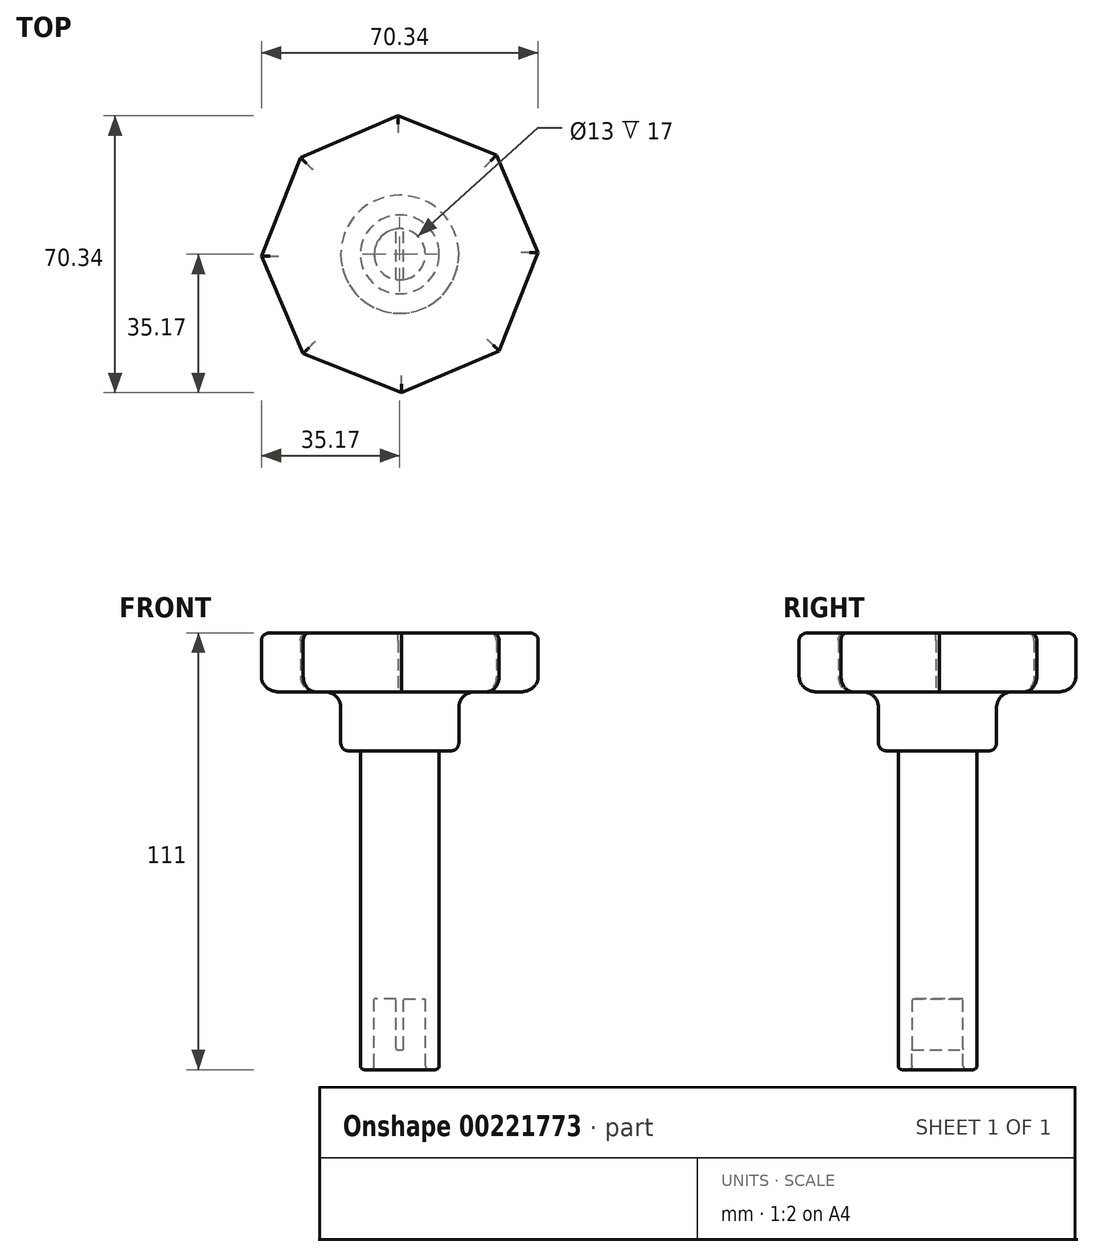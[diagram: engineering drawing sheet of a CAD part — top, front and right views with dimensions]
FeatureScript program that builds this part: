
annotation { "Feature Type Name" : "Feature", "Feature Type Description" : "" }
export const myFeature = defineFeature(function(context is Context, id is Id, definition is map)
    precondition{}
    {
        {
            var Q0;
            Q0=qCreatedBy(makeId("Top.planeOp"),FACE);
            var sketch = newSketch(context, id + "F0", { "sketchPlane" : qUnion([Q0])});
            skCircle(sketch, "E0.cCircle", {"center": v(0, 0) * mm, "radius": 32.5 * mm, "construction": true});
            skLineSegment(sketch, "E0.0", {"start": v(-25.21, 24.53) * mm, "end": v(-0.48, 35.17) * mm});
            skLineSegment(sketch, "E0.1", {"start": v(-0.48, 35.17) * mm, "end": v(24.53, 25.21) * mm});
            skLineSegment(sketch, "E0.2", {"start": v(24.53, 25.21) * mm, "end": v(35.17, 0.48) * mm});
            skLineSegment(sketch, "E0.3", {"start": v(35.17, 0.48) * mm, "end": v(25.21, -24.53) * mm});
            skLineSegment(sketch, "E0.4", {"start": v(25.21, -24.53) * mm, "end": v(0.48, -35.17) * mm});
            skLineSegment(sketch, "E0.5", {"start": v(0.48, -35.17) * mm, "end": v(-24.53, -25.21) * mm});
            skLineSegment(sketch, "E0.6", {"start": v(-24.53, -25.21) * mm, "end": v(-35.17, -0.48) * mm});
            skLineSegment(sketch, "E0.7", {"start": v(-35.17, -0.48) * mm, "end": v(-25.21, 24.53) * mm});
            skPoint(sketch, "E0.0.midPoint", {"position": v(-12.85, 29.85) * mm});
            skSolve(sketch);
        }
        {
            var Q0;
            Q0 = qSketchRegion(id + "F0", true);
            extrude(context, id + "F1", {"entities" : qUnion([Q0]), "depth" : 15 * mm});
        }
        {
            var Q0;
            Q0=makeQuery(id+"F1.opExtrude","CAP_FACE",FACE,{"disambiguationData":[OSD([sQuery(id+"F0.wireOp",EDGE,"E0.0"),sQuery(id+"F0.wireOp",EDGE,"E0.1"),sQuery(id+"F0.wireOp",EDGE,"E0.2"),sQuery(id+"F0.wireOp",EDGE,"E0.3"),sQuery(id+"F0.wireOp",EDGE,"E0.4"),sQuery(id+"F0.wireOp",EDGE,"E0.5"),sQuery(id+"F0.wireOp",EDGE,"E0.6"),sQuery(id+"F0.wireOp",EDGE,"E0.7")])],"isStart":true});
            var sketch = newSketch(context, id + "F2", { "sketchPlane" : qUnion([Q0])});
            skCircle(sketch, "E1", {"center": v(0, 0) * mm, "radius": 15 * mm});
            skSolve(sketch);
        }
        {
            var Q0;
            Q0 = qSketchRegion(id + "F2", true);
            extrude(context, id + "F3", {"entities" : qUnion([Q0]), "operationType" : NewBodyOperationType.ADD, "depth" : 15 * mm});
        }
        {
            var Q0;
            Q0=makeQuery(id+"F3.opExtrude","CAP_FACE",FACE,{"disambiguationData":[OSD([sQuery(id+"F2.wireOp",EDGE,"E1")])],"isStart":false});
            var sketch = newSketch(context, id + "F4", { "sketchPlane" : qUnion([Q0])});
            skCircle(sketch, "E2", {"center": v(0, 0) * mm, "radius": 10 * mm});
            skSolve(sketch);
        }
        {
            var Q0;
            Q0 = qSketchRegion(id + "F4", true);
            extrude(context, id + "F5", {"entities" : qUnion([Q0]), "operationType" : NewBodyOperationType.ADD, "depth" : 63 * mm});
        }
        {
            var Q0;
            Q0=makeQuery(id+"F5.opExtrude","CAP_EDGE",EDGE,{"disambiguationData":[OSD([sQuery(id+"F4.wireOp",EDGE,"E2")])],"isStart":true});
            var Q1;
            Q1=makeQuery(id+"F3.opExtrude","CAP_EDGE",EDGE,{"disambiguationData":[OSD([sQuery(id+"F2.wireOp",EDGE,"E1")])],"isStart":true});
            var Q2;
            Q2=makeQuery(id+"F1.opExtrude","CAP_FACE",FACE,{"disambiguationData":[OSD([sQuery(id+"F0.wireOp",EDGE,"E0.0"),sQuery(id+"F0.wireOp",EDGE,"E0.1"),sQuery(id+"F0.wireOp",EDGE,"E0.2"),sQuery(id+"F0.wireOp",EDGE,"E0.3"),sQuery(id+"F0.wireOp",EDGE,"E0.4"),sQuery(id+"F0.wireOp",EDGE,"E0.5"),sQuery(id+"F0.wireOp",EDGE,"E0.6"),sQuery(id+"F0.wireOp",EDGE,"E0.7")])],"isStart":true});
            fillet(context, id + "F6", {"entities" : qUnion([Q0, Q1, Q2]), "radius" : 4 * mm, "tangentPropagation" : true, "allowEdgeOverflow" : false});
        }
        {
            var Q0;
            Q0=makeQuery(id+"F1.opExtrude","CAP_FACE",FACE,{"disambiguationData":[OSD([sQuery(id+"F0.wireOp",EDGE,"E0.0"),sQuery(id+"F0.wireOp",EDGE,"E0.1"),sQuery(id+"F0.wireOp",EDGE,"E0.2"),sQuery(id+"F0.wireOp",EDGE,"E0.3"),sQuery(id+"F0.wireOp",EDGE,"E0.4"),sQuery(id+"F0.wireOp",EDGE,"E0.5"),sQuery(id+"F0.wireOp",EDGE,"E0.6"),sQuery(id+"F0.wireOp",EDGE,"E0.7")])],"isStart":false});
            var Q1;
            Q1=makeQuery(id+"F3.opExtrude","CAP_EDGE",EDGE,{"disambiguationData":[OSD([sQuery(id+"F2.wireOp",EDGE,"E1")])],"isStart":false});
            var Q2;
            Q2=makeQuery(id+"F3EO1j2PEONOvXl_1.opExtrude","CAP_EDGE",EDGE,{"disambiguationData":[OSD([sQuery(id+"FHGhLy2Cv9YmLs6_1.wireOp",EDGE,"M5NOvIKt-BTWJ-fP4f-TuiR-eHwRUutZLKey")])],"isStart":false});
            fillet(context, id + "F7", {"entities" : qUnion([Q0, Q1, Q2]), "radius" : 2 * mm, "tangentPropagation" : true, "allowEdgeOverflow" : false});
        }
        {
            var Q0;
            Q0=makeQuery(id+"F5.opExtrude","CAP_FACE",FACE,{"disambiguationData":[OSD([sQuery(id+"F4.wireOp",EDGE,"E2")])],"isStart":false});
            var sketch = newSketch(context, id + "F8", { "sketchPlane" : qUnion([Q0])});
            skCircle(sketch, "E3", {"center": v(0, 0) * mm, "radius": 10 * mm});
            skArc(sketch, "E4", {"start": v(-1, 6.42) * mm, "mid": v(-6.5, 0) * mm, "end": v(-1, -6.42) * mm});
            skLineSegment(sketch, "E5", {"start": v(-1, 6.42) * mm, "end": v(-1, -6.42) * mm});
            skLineSegment(sketch, "E6", {"start": v(1, 6.42) * mm, "end": v(1, -6.42) * mm});
            skArc(sketch, "E7.trimOffspring", {"start": v(1, -6.42) * mm, "mid": v(6.5, 0) * mm, "end": v(1, 6.42) * mm});
            skSolve(sketch);
        }
        {
            var Q0;
            Q0 = qSketchRegion(id + "F8", true);
            extrude(context, id + "F9", {"entities" : qUnion([Q0]), "operationType" : NewBodyOperationType.ADD, "depth" : 13 * mm});
        }
        {
            var Q0;
            Q0=makeQuery(id+"F9.opExtrude","CAP_EDGE",EDGE,{"disambiguationData":[OSD([sQuery(id+"F8.wireOp",EDGE,"E6")])],"isStart":false});
            var Q1;
            Q1=makeQuery(id+"F9.opExtrude","CAP_EDGE",EDGE,{"disambiguationData":[OSD([sQuery(id+"F8.wireOp",EDGE,"E5")])],"isStart":false});
            fillet(context, id + "F10", {"entities" : qUnion([Q0, Q1]), "radius" : .5 * mm, "tangentPropagation" : true, "allowEdgeOverflow" : false});
        }
        {
            var Q0;
            Q0=makeQuery(id+"F9.opExtrude","CAP_FACE",FACE,{"disambiguationData":[OSD([sQuery(id+"F8.wireOp",EDGE,"E3"),sQuery(id+"F8.wireOp",EDGE,"E4"),sQuery(id+"F8.wireOp",EDGE,"E5"),sQuery(id+"F8.wireOp",EDGE,"E6"),sQuery(id+"F8.wireOp",EDGE,"E7.trimOffspring")])],"isStart":false});
            var sketch = newSketch(context, id + "F11", { "sketchPlane" : qUnion([Q0])});
            skCircle(sketch, "E8", {"center": v(0, 0) * mm, "radius": 10 * mm});
            skCircle(sketch, "E9", {"center": v(0, 0) * mm, "radius": 6.5 * mm});
            skSolve(sketch);
        }
        {
            var Q0;
            Q0 = qSketchRegion(id + "F11", true);
            extrude(context, id + "F12", {"entities" : qUnion([Q0]), "operationType" : NewBodyOperationType.ADD, "depth" : 5 * mm});
        }
        {
            var Q0;
            Q0=makeQuery(id+"F12.opExtrude","CAP_FACE",FACE,{"disambiguationData":[OSD([sQuery(id+"F11.wireOp",EDGE,"E8"),sQuery(id+"F11.wireOp",EDGE,"E9")])],"isStart":false});
            fillet(context, id + "F13", {"entities" : qUnion([Q0]), "radius" : 1 * mm, "tangentPropagation" : true, "allowEdgeOverflow" : false});
        }
    });
